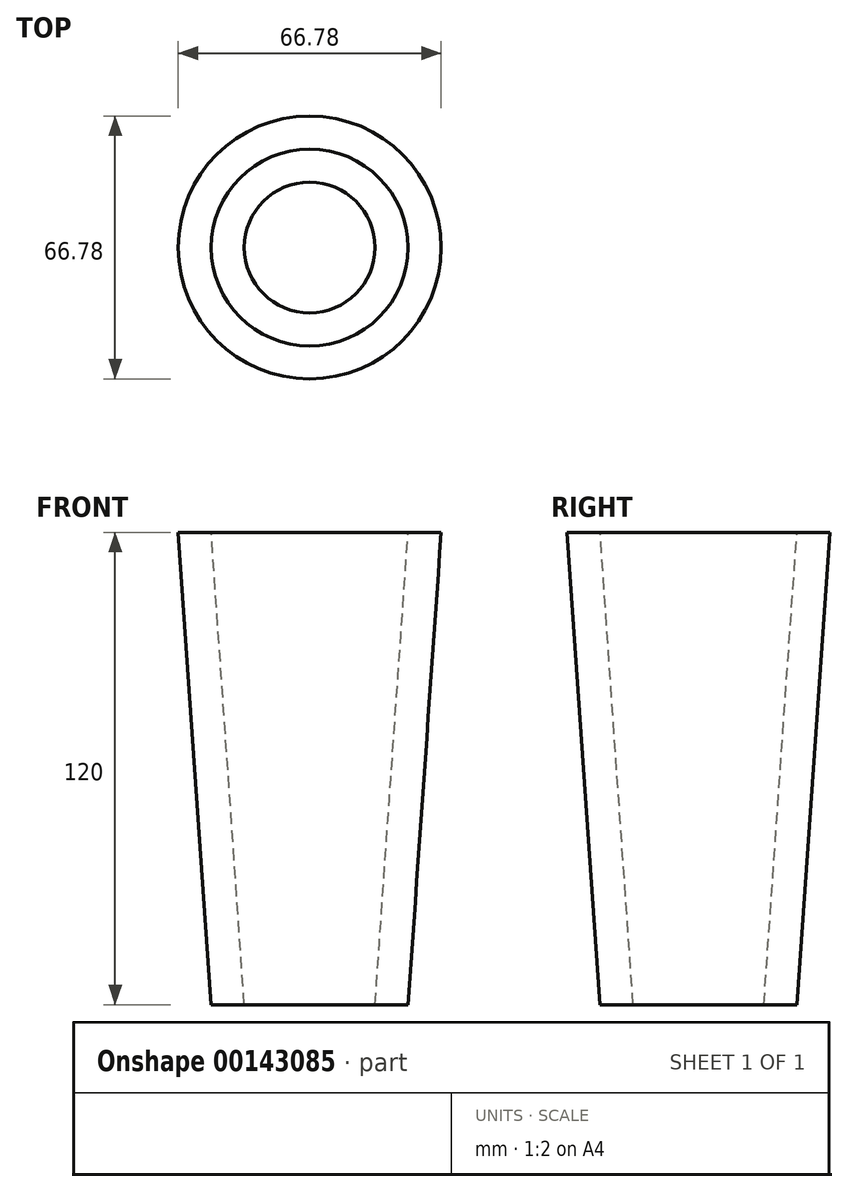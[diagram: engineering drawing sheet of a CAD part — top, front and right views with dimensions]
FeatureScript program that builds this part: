
annotation { "Feature Type Name" : "Feature", "Feature Type Description" : "" }
export const myFeature = defineFeature(function(context is Context, id is Id, definition is map)
    precondition{}
    {
        {
            var Q0;
            Q0=qCreatedBy(makeId("Top.planeOp"),FACE);
            var sketch = newSketch(context, id + "F0", { "sketchPlane" : qUnion([Q0])});
            skCircle(sketch, "E0", {"center": v(-9, 11.19) * mm, "radius": 25 * mm});
            skSolve(sketch);
        }
        {
            var Q0;
            Q0=makeQuery(id+"F0.imprint","IMPRINT",FACE,{"disambiguationData":[TD([[makeQuery(id+"F0.imprint","IMPRINT",EDGE,{"derivedFrom":sQuery(id+"F0.wireOp",EDGE,"E0")}),1.0]])]});
            extrude(context, id + "F1", {"entities" : qUnion([Q0]), "depth" : 120 * mm, "hasDraft" : true, "draftAngle" : 4 * degree});
        }
        {
            var Q0;
            Q0=makeQuery(id+"F1.opExtrude","CAP_FACE",FACE,{"disambiguationData":[OSD([sQuery(id+"F0.wireOp",EDGE,"E0")])],"isStart":false});
            var sketch = newSketch(context, id + "F2", { "sketchPlane" : qUnion([Q0])});
            skCircle(sketch, "E1.0.0", {"center": v(-9, 11.19) * mm, "radius": 33.4 * mm});
            skCircle(sketch, "E2", {"center": v(-9, 11.19) * mm, "radius": 25 * mm});
            skSolve(sketch);
        }
        {
            var Q0;
            Q0=makeQuery(id+"F2.imprint","IMPRINT",FACE,{"disambiguationData":[TD([[makeQuery(id+"F2.imprint","IMPRINT",EDGE,{"derivedFrom":sQuery(id+"F2.wireOp",EDGE,"E2")}),1.0]])]});
            extrude(context, id + "F3", {"entities" : qUnion([Q0]), "operationType" : NewBodyOperationType.REMOVE, "endBound" : BoundingType.UP_TO_NEXT, "oppositeDirection" : true, "depth" : 110 * mm, "hasDraft" : true, "draftAngle" : 4 * degree, "draftPullDirection" : true});
        }
    });
